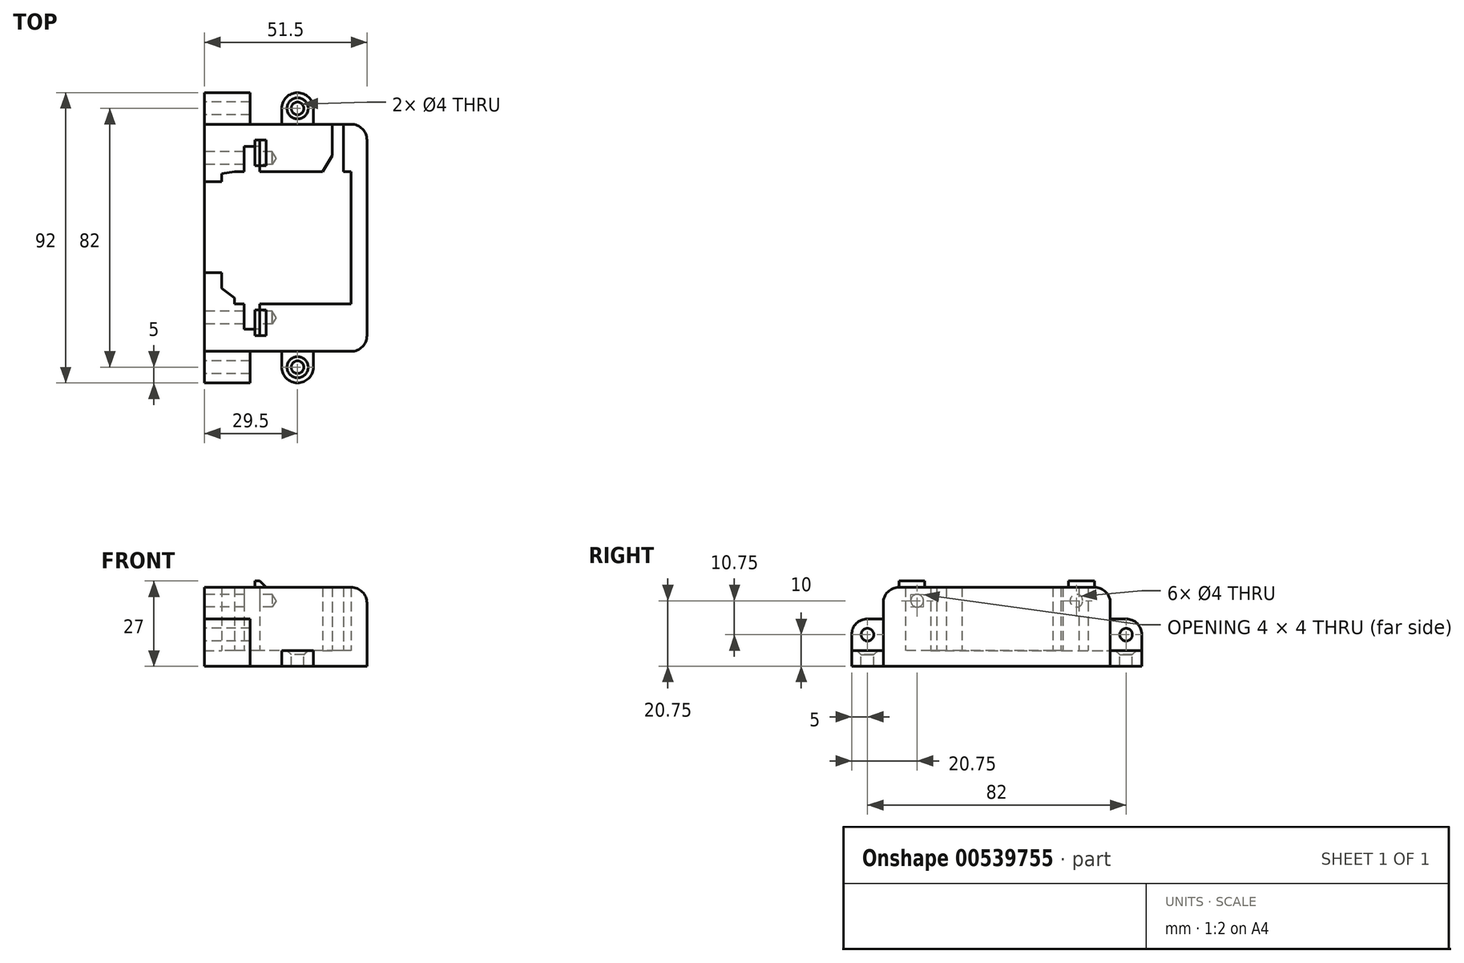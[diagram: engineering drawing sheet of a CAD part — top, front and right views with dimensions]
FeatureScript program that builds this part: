
annotation { "Feature Type Name" : "Feature", "Feature Type Description" : "" }
export const myFeature = defineFeature(function(context is Context, id is Id, definition is map)
    precondition{}
    {
        {
            var Q0;
            Q0=qCreatedBy(makeId("Top.planeOp"),FACE);
            var sketch = newSketch(context, id + "F0", { "sketchPlane" : qUnion([Q0])});
            skLineSegment(sketch, "E0.bottom", {"start": v(23.5, -36) * mm, "end": v(-23.5, -36) * mm});
            skLineSegment(sketch, "E0.top", {"start": v(23.5, 36) * mm, "end": v(-23.5, 36) * mm});
            skLineSegment(sketch, "E0.left", {"start": v(23.5, -36) * mm, "end": v(23.5, 36) * mm});
            skLineSegment(sketch, "E0.right", {"start": v(-23.5, -36) * mm, "end": v(-23.5, 0) * mm});
            skPoint(sketch, "E0.middle", {"position": v(0, 0) * mm});
            skLineSegment(sketch, "E1.bottom", {"start": v(18.5, -21) * mm, "end": v(-18.5, -21) * mm});
            skLineSegment(sketch, "E1.top", {"start": v(9.5, 21) * mm, "end": v(-18.5, 21) * mm});
            skLineSegment(sketch, "E1.left", {"start": v(18.5, -21) * mm, "end": v(18.5, 21) * mm});
            skLineSegment(sketch, "E1.right", {"start": v(-18.5, -21) * mm, "end": v(-18.5, 21) * mm, "construction": true});
            skLineSegment(sketch, "E2.right", {"start": v(12.5, 26) * mm, "end": v(12.5, 36) * mm});
            skLineSegment(sketch, "E3", {"start": v(-23.5, 0) * mm, "end": v(23.5, 0) * mm, "construction": true});
            skLineSegment(sketch, "E4.bottom", {"start": v(-10.5, 21) * mm, "end": v(-15.5, 21) * mm});
            skLineSegment(sketch, "E4.top", {"start": v(-10.5, 29) * mm, "end": v(-15.5, 29) * mm});
            skLineSegment(sketch, "E4.left", {"start": v(-10.5, 21) * mm, "end": v(-10.5, 29) * mm});
            skLineSegment(sketch, "E4.right", {"start": v(-15.5, 21) * mm, "end": v(-15.5, 29) * mm});
            skLineSegment(sketch, "E5.bottom", {"start": v(-10.5, -21) * mm, "end": v(-15.5, -21) * mm});
            skLineSegment(sketch, "E5.top", {"start": v(-10.5, -29) * mm, "end": v(-15.5, -29) * mm});
            skLineSegment(sketch, "E5.left", {"start": v(-10.5, -21) * mm, "end": v(-10.5, -29) * mm});
            skLineSegment(sketch, "E5.right", {"start": v(-15.5, -21) * mm, "end": v(-15.5, -29) * mm});
            skLineSegment(sketch, "E6.bottom", {"start": v(-18.5, 21) * mm, "end": v(-22.5, 20.3) * mm});
            skLineSegment(sketch, "E6.right", {"start": v(-22.5, 20.3) * mm, "end": v(-22.5, 17.8) * mm});
            skLineSegment(sketch, "E7", {"start": v(-22.5, -16) * mm, "end": v(-18.5, -19) * mm});
            skLineSegment(sketch, "E8.bottom", {"start": v(-23.5, 17.8) * mm, "end": v(-22.5, 17.8) * mm});
            skLineSegment(sketch, "E8.top", {"start": v(-23.5, -11) * mm, "end": v(-22.5, -11) * mm});
            skLineSegment(sketch, "E8.left", {"start": v(-23.5, 17.8) * mm, "end": v(-23.5, -11) * mm});
            skLineSegment(sketch, "E8.right", {"start": v(-22.5, 17.8) * mm, "end": v(-22.5, -11) * mm});
            skLineSegment(sketch, "E9.trimOffspring", {"start": v(-23.5, 17.8) * mm, "end": v(-23.5, 36) * mm});
            skLineSegment(sketch, "E10.trimOffspring", {"start": v(-22.5, 0) * mm, "end": v(-22.5, -16) * mm});
            skLineSegment(sketch, "E11", {"start": v(-18.5, -19) * mm, "end": v(-18.5, -21) * mm});
            skLineSegment(sketch, "E12", {"start": v(9.5, 21) * mm, "end": v(12.5, 26) * mm});
            skLineSegment(sketch, "E13", {"start": v(18.5, 21) * mm, "end": v(16, 21) * mm});
            skLineSegment(sketch, "E14", {"start": v(16, 21) * mm, "end": v(16, 36) * mm});
            skSolve(sketch);
        }
        {
            var Q0;
            Q0=makeQuery(id+"F0.imprint","IMPRINT",FACE,{"disambiguationData":[TD([[makeQuery(id+"F0.imprint","IMPRINT",EDGE,{"derivedFrom":sQuery(id+"F0.wireOp",EDGE,"E0.bottom")}),-1.0]])]});
            var Q1;
            {var subQ5=sQuery(id+"F0.wireOp",EDGE,"E2.right");Q1=makeQuery(id+"F0.imprint","IMPRINT",FACE,{"disambiguationData":[TD([[makeQuery(id+"F0.imprint","IMPRINT",EDGE,{"derivedFrom":subQ5}),1.0]])]});}
            extrude(context, id + "F1", {"entities" : qUnion([Q0, Q1]), "depth" : 20 * mm, "offsetDistance" : 25 * mm});
        }
        {
            var Q0;
            {var subQ2=sQuery(id+"F0.wireOp",EDGE,"E1.left");Q0=makeQuery(id+"F0.imprint","IMPRINT",FACE,{"disambiguationData":[TD([[makeQuery(id+"F0.imprint","IMPRINT",EDGE,{"derivedFrom":subQ2}),1.0]])]});}
            var sketch = newSketch(context, id + "F2", { "sketchPlane" : qUnion([Q0])});
            skLineSegment(sketch, "E15.bottom", {"start": v(23.5, 36) * mm, "end": v(-23.5, 36) * mm});
            skLineSegment(sketch, "E15.top", {"start": v(23.5, -36) * mm, "end": v(-23.5, -36) * mm});
            skLineSegment(sketch, "E15.left", {"start": v(23.5, 36) * mm, "end": v(23.5, -36) * mm});
            skLineSegment(sketch, "E15.right", {"start": v(-23.5, 36) * mm, "end": v(-23.5, -36) * mm});
            skPoint(sketch, "E15.middle", {"position": v(0, 0) * mm});
            skSolve(sketch);
        }
        {
            var Q0;
            Q0=makeQuery(id+"F2.imprint","IMPRINT",FACE,{"disambiguationData":[TD([[makeQuery(id+"F2.imprint","IMPRINT",EDGE,{"derivedFrom":sQuery(id+"F2.wireOp",EDGE,"E15.bottom")}),1.0]])]});
            var Q1;
            {var subQ3=sQuery(id+"F0.wireOp",EDGE,"E1.left");Q1=makeQuery(id+"F2.imprint","IMPRINT",FACE,{"disambiguationData":[TD([[makeQuery(id+"F2.imprint","IMPRINT",EDGE,{"derivedFrom":makeQuery(id+"F0.imprint","IMPRINT",EDGE,{"derivedFrom":subQ3})}),1.0]])]});}
            extrude(context, id + "F3", {"entities" : qUnion([Q0, Q1]), "oppositeDirection" : true, "depth" : 5 * mm, "offsetDistance" : 25 * mm});
        }
        {
            var Q0;
            Q0=makeQuery(id+"F1.opExtrude","SWEPT_BODY",BODY,{"disambiguationData":[OSD([sQuery(id+"F0.wireOp",EDGE,"E0.top"),sQuery(id+"F0.wireOp",EDGE,"E1.top"),sQuery(id+"F0.wireOp",EDGE,"E2.right"),sQuery(id+"F0.wireOp",EDGE,"E4.top"),sQuery(id+"F0.wireOp",EDGE,"E4.left"),sQuery(id+"F0.wireOp",EDGE,"E4.right"),sQuery(id+"F0.wireOp",EDGE,"E6.bottom"),sQuery(id+"F0.wireOp",EDGE,"E6.right"),sQuery(id+"F0.wireOp",EDGE,"E8.bottom"),sQuery(id+"F0.wireOp",EDGE,"E9.trimOffspring")])]});
            var Q1;
            Q1=makeQuery(id+"F3.opExtrude","SWEPT_BODY",BODY,{"disambiguationData":[OSD([sQuery(id+"F2.wireOp",EDGE,"E15.bottom"),sQuery(id+"F2.wireOp",EDGE,"E15.top"),sQuery(id+"F2.wireOp",EDGE,"E15.left"),sQuery(id+"F2.wireOp",EDGE,"E15.right")])]});
            var Q2;
            Q2=makeQuery(id+"F1.opExtrude","SWEPT_BODY",BODY,{"disambiguationData":[OSD([sQuery(id+"F0.wireOp",EDGE,"E0.bottom"),sQuery(id+"F0.wireOp",EDGE,"E0.top"),sQuery(id+"F0.wireOp",EDGE,"E0.left"),sQuery(id+"F0.wireOp",EDGE,"E0.right"),sQuery(id+"F0.wireOp",EDGE,"E1.bottom"),sQuery(id+"F0.wireOp",EDGE,"E1.left"),sQuery(id+"F0.wireOp",EDGE,"E2.left"),sQuery(id+"F0.wireOp",EDGE,"E5.top"),sQuery(id+"F0.wireOp",EDGE,"E5.left"),sQuery(id+"F0.wireOp",EDGE,"E5.right"),sQuery(id+"F0.wireOp",EDGE,"E7"),sQuery(id+"F0.wireOp",EDGE,"E8.top"),sQuery(id+"F0.wireOp",EDGE,"E10.trimOffspring"),sQuery(id+"F0.wireOp",EDGE,"E11")])]});
            booleanBodies(context, id + "F4", {"operationType" : BooleanOperationType.UNION, "tools" : qUnion([Q0, Q1, Q2])});
        }
        {
            var Q0;
            Q0=makeQuery(id+"F4.opBoolean","MERGE",FACE,{"derivedFrom":[makeQuery(id+"F1.opExtrude","SWEPT_FACE",FACE,{"disambiguationData":[OSD([sQuery(id+"F0.wireOp",EDGE,"E0.bottom")])]}),makeQuery(id+"F3.opExtrude","SWEPT_FACE",FACE,{"disambiguationData":[OSD([sQuery(id+"F2.wireOp",EDGE,"E15.top")])]})]});
            var sketch = newSketch(context, id + "F5", { "sketchPlane" : qUnion([Q0])});
            skLineSegment(sketch, "E16.bottom", {"start": v(-23.5, -5) * mm, "end": v(-13.5, -5) * mm});
            skLineSegment(sketch, "E16.top", {"start": v(-23.5, 10) * mm, "end": v(-13.5, 10) * mm});
            skLineSegment(sketch, "E16.left", {"start": v(-23.5, -5) * mm, "end": v(-23.5, 10) * mm});
            skLineSegment(sketch, "E16.right", {"start": v(-13.5, -5) * mm, "end": v(-13.5, 10) * mm});
            skSolve(sketch);
        }
        {
            var Q0;
            Q0=makeQuery(id+"F5.imprint","IMPRINT",FACE,{"disambiguationData":[TD([[makeQuery(id+"F5.imprint","IMPRINT",EDGE,{"derivedFrom":sQuery(id+"F5.wireOp",EDGE,"E16.bottom")}),-1.0]])]});
            extrude(context, id + "F6", {"entities" : qUnion([Q0]), "operationType" : NewBodyOperationType.ADD, "depth" : 10 * mm, "offsetDistance" : 25 * mm});
        }
        {
            var Q0;
            Q0=makeQuery(id+"F6.opExtrude","CAP_EDGE",EDGE,{"disambiguationData":[OSD([sQuery(id+"F5.wireOp",EDGE,"E16.top")])],"isStart":false});
            fillet(context, id + "F7", {"entities" : qUnion([Q0]), "radius" : 5 * mm, "tangentPropagation" : true, "allowEdgeOverflow" : false});
        }
        {
            var Q0;
            {var subQ0=sQuery(id+"F0.wireOp",EDGE,"E0.top");Q0=makeQuery(id+"F4.opBoolean","MERGE",FACE,{"derivedFrom":[makeQuery(id+"F1.opExtrude","SWEPT_FACE",FACE,{"disambiguationData":[OSD([subQ0]),TDD([makeQuery(id+"F0.imprint","IMPRINT",EDGE,{"disambiguationData":[TD([[makeQuery(id+"F0.imprint","INTERSECT",VERTEX,{"derivedFrom":[subQ0,sQuery(id+"F0.wireOp",EDGE,"E0.left")]}),-1.0]])],"derivedFrom":subQ0})])]}),makeQuery(id+"F1.opExtrude","SWEPT_FACE",FACE,{"disambiguationData":[OSD([subQ0]),TDD([makeQuery(id+"F0.imprint","IMPRINT",EDGE,{"disambiguationData":[TD([[makeQuery(id+"F0.imprint","INTERSECT",VERTEX,{"derivedFrom":[subQ0,sQuery(id+"F0.wireOp",EDGE,"E9.trimOffspring")]}),1.0]])],"derivedFrom":subQ0})])]}),makeQuery(id+"F3.opExtrude","SWEPT_FACE",FACE,{"disambiguationData":[OSD([sQuery(id+"F2.wireOp",EDGE,"E15.bottom")])]})]});}
            var sketch = newSketch(context, id + "F8", { "sketchPlane" : qUnion([Q0])});
            skLineSegment(sketch, "E17.bottom", {"start": v(23.5, -5) * mm, "end": v(13.5, -5) * mm});
            skLineSegment(sketch, "E17.top", {"start": v(23.5, 10) * mm, "end": v(13.5, 10) * mm});
            skLineSegment(sketch, "E17.left", {"start": v(23.5, -5) * mm, "end": v(23.5, 10) * mm});
            skLineSegment(sketch, "E17.right", {"start": v(13.5, -5) * mm, "end": v(13.5, 10) * mm});
            skSolve(sketch);
        }
        {
            var Q0;
            Q0=makeQuery(id+"F8.imprint","IMPRINT",FACE,{"disambiguationData":[TD([[makeQuery(id+"F8.imprint","IMPRINT",EDGE,{"derivedFrom":sQuery(id+"F8.wireOp",EDGE,"E17.bottom")}),1.0]])]});
            extrude(context, id + "F9", {"entities" : qUnion([Q0]), "operationType" : NewBodyOperationType.ADD, "depth" : 10 * mm, "offsetDistance" : 25 * mm});
        }
        {
            var Q0;
            Q0=makeQuery(id+"F9.opExtrude","CAP_EDGE",EDGE,{"disambiguationData":[OSD([sQuery(id+"F8.wireOp",EDGE,"E17.top")])],"isStart":false});
            fillet(context, id + "F10", {"entities" : qUnion([Q0]), "radius" : 5 * mm, "tangentPropagation" : true, "allowEdgeOverflow" : false});
        }
        {
            var Q0;
            Q0=makeQuery(id+"F9.boolean.opBoolean","MERGE",FACE,{"derivedFrom":[makeQuery(id+"F6.boolean.opBoolean","MERGE",FACE,{"derivedFrom":[makeQuery(id+"F4.opBoolean","MERGE",FACE,{"derivedFrom":[makeQuery(id+"F1.opExtrude","SWEPT_FACE",FACE,{"disambiguationData":[OSD([sQuery(id+"F0.wireOp",EDGE,"E0.right")])]}),makeQuery(id+"F1.opExtrude","SWEPT_FACE",FACE,{"disambiguationData":[OSD([sQuery(id+"F0.wireOp",EDGE,"E9.trimOffspring")])]}),makeQuery(id+"F3.opExtrude","SWEPT_FACE",FACE,{"disambiguationData":[OSD([sQuery(id+"F2.wireOp",EDGE,"E15.right")])]})]}),makeQuery(id+"F6.opExtrude","SWEPT_FACE",FACE,{"disambiguationData":[OSD([sQuery(id+"F5.wireOp",EDGE,"E16.left")])]})]}),makeQuery(id+"F9.opExtrude","SWEPT_FACE",FACE,{"disambiguationData":[OSD([sQuery(id+"F8.wireOp",EDGE,"E17.left")])]})]});
            var sketch = newSketch(context, id + "F11", { "sketchPlane" : qUnion([Q0])});
            skPoint(sketch, "E18", {"position": v(-41, 5) * mm});
            skPoint(sketch, "E19", {"position": v(41, 5) * mm});
            skSolve(sketch);
        }
        {
            var Q0;
            Q0=sQuery(id+"F11.wireOp",VERTEX,"E18");
            var Q1;
            Q1=sQuery(id+"F11.wireOp",VERTEX,"E19");
            var Q2;
            Q2=makeQuery(id+"F1.opExtrude","SWEPT_BODY",BODY,{"disambiguationData":[OSD([sQuery(id+"F0.wireOp",EDGE,"E0.top"),sQuery(id+"F0.wireOp",EDGE,"E1.top"),sQuery(id+"F0.wireOp",EDGE,"E2.right"),sQuery(id+"F0.wireOp",EDGE,"E4.top"),sQuery(id+"F0.wireOp",EDGE,"E4.left"),sQuery(id+"F0.wireOp",EDGE,"E4.right"),sQuery(id+"F0.wireOp",EDGE,"E6.bottom"),sQuery(id+"F0.wireOp",EDGE,"E6.right"),sQuery(id+"F0.wireOp",EDGE,"E8.bottom"),sQuery(id+"F0.wireOp",EDGE,"E9.trimOffspring")])]});
            hole(context, id + "F12", {"style" : HoleStyle.SIMPLE, "endStyle" : HoleEndStyle.THROUGH, "holeDiameter" : 4 * mm, "isTappedThrough" : true, "tappedDepth" : 12 * mm, "tapClearance" : 3, "locations" : qUnion([Q0, Q1]), "scope" : qUnion([Q2])});
        }
        {
            var Q0;
            Q0=makeQuery(id+"F9.boolean.opBoolean","MERGE",FACE,{"derivedFrom":[makeQuery(id+"F6.boolean.opBoolean","MERGE",FACE,{"derivedFrom":[makeQuery(id+"F4.opBoolean","MERGE",FACE,{"derivedFrom":[makeQuery(id+"F1.opExtrude","SWEPT_FACE",FACE,{"disambiguationData":[OSD([sQuery(id+"F0.wireOp",EDGE,"E0.right")])]}),makeQuery(id+"F1.opExtrude","SWEPT_FACE",FACE,{"disambiguationData":[OSD([sQuery(id+"F0.wireOp",EDGE,"E9.trimOffspring")])]}),makeQuery(id+"F3.opExtrude","SWEPT_FACE",FACE,{"disambiguationData":[OSD([sQuery(id+"F2.wireOp",EDGE,"E15.right")])]})]}),makeQuery(id+"F6.opExtrude","SWEPT_FACE",FACE,{"disambiguationData":[OSD([sQuery(id+"F5.wireOp",EDGE,"E16.left")])]})]}),makeQuery(id+"F9.opExtrude","SWEPT_FACE",FACE,{"disambiguationData":[OSD([sQuery(id+"F8.wireOp",EDGE,"E17.left")])]})]});
            var sketch = newSketch(context, id + "F13", { "sketchPlane" : qUnion([Q0])});
            skPoint(sketch, "E20", {"position": v(25.25, 15.75) * mm});
            skPoint(sketch, "E21", {"position": v(-25.25, 15.75) * mm});
            skSolve(sketch);
        }
        {
            var Q0;
            Q0=sQuery(id+"F13.wireOp",VERTEX,"E21");
            var Q1;
            Q1=sQuery(id+"F13.wireOp",VERTEX,"E20");
            var Q2;
            Q2=makeQuery(id+"F1.opExtrude","SWEPT_BODY",BODY,{"disambiguationData":[OSD([sQuery(id+"F0.wireOp",EDGE,"E0.top"),sQuery(id+"F0.wireOp",EDGE,"E1.top"),sQuery(id+"F0.wireOp",EDGE,"E2.right"),sQuery(id+"F0.wireOp",EDGE,"E4.top"),sQuery(id+"F0.wireOp",EDGE,"E4.left"),sQuery(id+"F0.wireOp",EDGE,"E4.right"),sQuery(id+"F0.wireOp",EDGE,"E6.bottom"),sQuery(id+"F0.wireOp",EDGE,"E6.right"),sQuery(id+"F0.wireOp",EDGE,"E8.bottom"),sQuery(id+"F0.wireOp",EDGE,"E9.trimOffspring")])]});
            hole(context, id + "F14", {"style" : HoleStyle.SIMPLE, "endStyle" : HoleEndStyle.BLIND, "holeDiameter" : 4 * mm, "holeDepth" : 17 * mm, "isTappedThrough" : true, "tappedDepth" : 12 * mm, "tapClearance" : 3, "locations" : qUnion([Q0, Q1]), "scope" : qUnion([Q2])});
        }
        {
            var Q0;
            {var subQ0=sQuery(id+"F0.wireOp",EDGE,"E0.top");Q0=makeQuery(id+"F1.opExtrude","CAP_EDGE",EDGE,{"disambiguationData":[OSD([subQ0]),TDD([makeQuery(id+"F0.imprint","IMPRINT",EDGE,{"disambiguationData":[TD([[makeQuery(id+"F0.imprint","INTERSECT",VERTEX,{"derivedFrom":[subQ0,sQuery(id+"F0.wireOp",EDGE,"E9.trimOffspring")]}),1.0]])],"derivedFrom":subQ0})])],"isStart":false});}
            var Q1;
            Q1=makeQuery(id+"F1.opExtrude","CAP_EDGE",EDGE,{"disambiguationData":[OSD([sQuery(id+"F0.wireOp",EDGE,"E0.bottom")])],"isStart":false});
            var Q2;
            Q2=makeQuery(id+"F1.opExtrude","CAP_EDGE",EDGE,{"disambiguationData":[OSD([sQuery(id+"F0.wireOp",EDGE,"E0.left")])],"isStart":false});
            fillet(context, id + "F15", {"entities" : qUnion([Q0, Q1, Q2]), "radius" : 5 * mm, "tangentPropagation" : true, "allowEdgeOverflow" : false});
        }
        {
            var Q0;
            {var subQ0=sQuery(id+"F0.wireOp",EDGE,"E0.top");var subQ1=sQuery(id+"F0.wireOp",EDGE,"E0.left");Q0=makeQuery(id+"F15.opFillet","BLEND_EDGE",EDGE,{"blendedFrom":[makeQuery(id+"F1.opExtrude","CAP_EDGE",EDGE,{"disambiguationData":[OSD([subQ1])],"isStart":false}),makeQuery(id+"F4.opBoolean","MERGE",FACE,{"derivedFrom":[makeQuery(id+"F1.opExtrude","SWEPT_FACE",FACE,{"disambiguationData":[OSD([subQ0]),TDD([makeQuery(id+"F0.imprint","IMPRINT",EDGE,{"disambiguationData":[TD([[makeQuery(id+"F0.imprint","INTERSECT",VERTEX,{"derivedFrom":[subQ0,subQ1]}),-1.0]])],"derivedFrom":subQ0})])]}),makeQuery(id+"F1.opExtrude","SWEPT_FACE",FACE,{"disambiguationData":[OSD([subQ0]),TDD([makeQuery(id+"F0.imprint","IMPRINT",EDGE,{"disambiguationData":[TD([[makeQuery(id+"F0.imprint","INTERSECT",VERTEX,{"derivedFrom":[subQ0,sQuery(id+"F0.wireOp",EDGE,"E9.trimOffspring")]}),1.0]])],"derivedFrom":subQ0})])]}),makeQuery(id+"F3.opExtrude","SWEPT_FACE",FACE,{"disambiguationData":[OSD([sQuery(id+"F2.wireOp",EDGE,"E15.bottom")])]})]})],"blendedInto":[makeQuery(id+"F4.opBoolean","MERGE",FACE,{"derivedFrom":[makeQuery(id+"F1.opExtrude","SWEPT_FACE",FACE,{"disambiguationData":[OSD([subQ0]),TDD([makeQuery(id+"F0.imprint","IMPRINT",EDGE,{"disambiguationData":[TD([[makeQuery(id+"F0.imprint","INTERSECT",VERTEX,{"derivedFrom":[subQ0,subQ1]}),-1.0]])],"derivedFrom":subQ0})])]}),makeQuery(id+"F1.opExtrude","SWEPT_FACE",FACE,{"disambiguationData":[OSD([subQ0]),TDD([makeQuery(id+"F0.imprint","IMPRINT",EDGE,{"disambiguationData":[TD([[makeQuery(id+"F0.imprint","INTERSECT",VERTEX,{"derivedFrom":[subQ0,sQuery(id+"F0.wireOp",EDGE,"E9.trimOffspring")]}),1.0]])],"derivedFrom":subQ0})])]}),makeQuery(id+"F3.opExtrude","SWEPT_FACE",FACE,{"disambiguationData":[OSD([sQuery(id+"F2.wireOp",EDGE,"E15.bottom")])]})]})]});}
            var Q1;
            Q1=makeQuery(id+"F15.opFillet","BLEND_EDGE",EDGE,{"blendedFrom":[makeQuery(id+"F1.opExtrude","CAP_EDGE",EDGE,{"disambiguationData":[OSD([sQuery(id+"F0.wireOp",EDGE,"E0.bottom")])],"isStart":false}),makeQuery(id+"F1.opExtrude","CAP_EDGE",EDGE,{"disambiguationData":[OSD([sQuery(id+"F0.wireOp",EDGE,"E0.left")])],"isStart":false})],"blendedInto":[]});
            fillet(context, id + "F16", {"entities" : qUnion([Q0, Q1]), "radius" : 5 * mm, "tangentPropagation" : true, "allowEdgeOverflow" : false});
        }
        {
            var Q0;
            Q0=makeQuery(id+"F15.opFillet","SPLIT",FACE,{"disambiguationData":[OD(0.0)],"derivedFrom":makeQuery(id+"F1.opExtrude","CAP_FACE",FACE,{"disambiguationData":[OSD([sQuery(id+"F0.wireOp",EDGE,"E0.bottom"),sQuery(id+"F0.wireOp",EDGE,"E0.top"),sQuery(id+"F0.wireOp",EDGE,"E0.left"),sQuery(id+"F0.wireOp",EDGE,"E0.right"),sQuery(id+"F0.wireOp",EDGE,"E1.bottom"),sQuery(id+"F0.wireOp",EDGE,"E1.left"),sQuery(id+"F0.wireOp",EDGE,"E5.top"),sQuery(id+"F0.wireOp",EDGE,"E5.left"),sQuery(id+"F0.wireOp",EDGE,"E5.right"),sQuery(id+"F0.wireOp",EDGE,"E7"),sQuery(id+"F0.wireOp",EDGE,"E8.top"),sQuery(id+"F0.wireOp",EDGE,"E10.trimOffspring"),sQuery(id+"F0.wireOp",EDGE,"E11"),sQuery(id+"F0.wireOp",EDGE,"E13"),sQuery(id+"F0.wireOp",EDGE,"E14")])],"isStart":false})});
            var sketch = newSketch(context, id + "F17", { "sketchPlane" : qUnion([Q0])});
            skLineSegment(sketch, "E22", {"start": v(0, 0) * mm, "end": v(57.27, 0) * mm, "construction": true});
            skLineSegment(sketch, "E23.bottom", {"start": v(-10.5, -22.8) * mm, "end": v(-8.5, -22.8) * mm});
            skLineSegment(sketch, "E23.top", {"start": v(-10.5, -31) * mm, "end": v(-8.5, -31) * mm});
            skLineSegment(sketch, "E23.left", {"start": v(-10.5, -22.8) * mm, "end": v(-10.5, -31) * mm});
            skLineSegment(sketch, "E23.right", {"start": v(-8.5, -22.8) * mm, "end": v(-8.5, -31) * mm});
            skLineSegment(sketch, "E24.MirrorCS", {"start": v(-10.5, 22.8) * mm, "end": v(-8.5, 22.8) * mm});
            skLineSegment(sketch, "E25.MirrorCS", {"start": v(-10.5, 22.8) * mm, "end": v(-10.5, 31) * mm});
            skLineSegment(sketch, "E26.MirrorCS", {"start": v(-10.5, 31) * mm, "end": v(-8.5, 31) * mm});
            skLineSegment(sketch, "E27.MirrorCS", {"start": v(-8.5, 22.8) * mm, "end": v(-8.5, 31) * mm});
            skLineSegment(sketch, "E28.0", {"start": v(-15.5, -21) * mm, "end": v(-15.5, -29) * mm});
            skLineSegment(sketch, "E29.0", {"start": v(-10.5, -21) * mm, "end": v(-10.5, -29) * mm});
            skSolve(sketch);
        }
        {
            var Q0;
            Q0=makeQuery(id+"F17.imprint","IMPRINT",FACE,{"disambiguationData":[TD([[makeQuery(id+"F17.imprint","IMPRINT",EDGE,{"derivedFrom":sQuery(id+"F17.wireOp",EDGE,"E23.bottom")}),-1.0]])]});
            var Q1;
            Q1=makeQuery(id+"F17.imprint","IMPRINT",FACE,{"disambiguationData":[TD([[makeQuery(id+"F17.imprint","IMPRINT",EDGE,{"derivedFrom":sQuery(id+"F17.wireOp",EDGE,"E24.MirrorCS")}),1.0]])]});
            extrude(context, id + "F18", {"entities" : qUnion([Q0, Q1]), "operationType" : NewBodyOperationType.ADD, "depth" : 2 * mm, "offsetDistance" : 25 * mm});
        }
        {
            var Q0;
            Q0=makeQuery(id+"F18.boolean.opBoolean","MERGE",FACE,{"derivedFrom":[makeQuery(id+"F1.opExtrude","SWEPT_FACE",FACE,{"disambiguationData":[OSD([sQuery(id+"F0.wireOp",EDGE,"E4.left")])]}),makeQuery(id+"F18.opExtrude","SWEPT_FACE",FACE,{"disambiguationData":[OSD([sQuery(id+"F17.wireOp",EDGE,"E25.MirrorCS")])]})]});
            var sketch = newSketch(context, id + "F19", { "sketchPlane" : qUnion([Q0])});
            skLineSegment(sketch, "E30.bottom", {"start": v(-31, 22) * mm, "end": v(-22.8, 22) * mm});
            skLineSegment(sketch, "E30.top", {"start": v(-31, 20) * mm, "end": v(-22.8, 20) * mm});
            skLineSegment(sketch, "E30.left", {"start": v(-31, 22) * mm, "end": v(-31, 20) * mm});
            skLineSegment(sketch, "E30.right", {"start": v(-22.8, 22) * mm, "end": v(-22.8, 20) * mm});
            skLineSegment(sketch, "E31.MirrorCS", {"start": v(22.8, 22) * mm, "end": v(22.8, 20) * mm});
            skLineSegment(sketch, "E32.MirrorCS", {"start": v(31, 22) * mm, "end": v(31, 20) * mm});
            skLineSegment(sketch, "E33.MirrorCS", {"start": v(31, 20) * mm, "end": v(22.8, 20) * mm});
            skLineSegment(sketch, "E34.MirrorCS", {"start": v(31, 22) * mm, "end": v(22.8, 22) * mm});
            skSolve(sketch);
        }
        {
            var Q0;
            Q0=makeQuery(id+"F19.imprint","IMPRINT",FACE,{"disambiguationData":[TD([[makeQuery(id+"F19.imprint","IMPRINT",EDGE,{"derivedFrom":sQuery(id+"F19.wireOp",EDGE,"E30.bottom")}),1.0]])]});
            var Q1;
            Q1=makeQuery(id+"F19.imprint","IMPRINT",FACE,{"disambiguationData":[TD([[makeQuery(id+"F19.imprint","IMPRINT",EDGE,{"derivedFrom":sQuery(id+"F19.wireOp",EDGE,"E31.MirrorCS")}),1.0]])]});
            extrude(context, id + "F20", {"entities" : qUnion([Q0, Q1]), "operationType" : NewBodyOperationType.ADD, "depth" : 1.5 * mm, "offsetDistance" : 25 * mm});
        }
        {
            var Q0;
            Q0=makeQuery(id+"F18.opExtrude","CAP_EDGE",EDGE,{"disambiguationData":[OSD([sQuery(id+"F17.wireOp",EDGE,"E23.right")])],"isStart":false});
            var Q1;
            Q1=makeQuery(id+"F18.opExtrude","CAP_EDGE",EDGE,{"disambiguationData":[OSD([sQuery(id+"F17.wireOp",EDGE,"E27.MirrorCS")])],"isStart":false});
            chamfer(context, id + "F21", {"entities" : qUnion([Q0, Q1]), "width" : 2 * mm, "tangentPropagation" : true});
        }
        {
            var Q0;
            Q0=makeQuery(id+"F9.boolean.opBoolean","MERGE",FACE,{"derivedFrom":[makeQuery(id+"F6.boolean.opBoolean","MERGE",FACE,{"derivedFrom":[makeQuery(id+"F4.opBoolean","MERGE",FACE,{"derivedFrom":[makeQuery(id+"F1.opExtrude","SWEPT_FACE",FACE,{"disambiguationData":[OSD([sQuery(id+"F0.wireOp",EDGE,"E0.right")])]}),makeQuery(id+"F1.opExtrude","SWEPT_FACE",FACE,{"disambiguationData":[OSD([sQuery(id+"F0.wireOp",EDGE,"E9.trimOffspring")])]}),makeQuery(id+"F3.opExtrude","SWEPT_FACE",FACE,{"disambiguationData":[OSD([sQuery(id+"F2.wireOp",EDGE,"E15.right")])]})]}),makeQuery(id+"F6.opExtrude","SWEPT_FACE",FACE,{"disambiguationData":[OSD([sQuery(id+"F5.wireOp",EDGE,"E16.left")])]})]}),makeQuery(id+"F9.opExtrude","SWEPT_FACE",FACE,{"disambiguationData":[OSD([sQuery(id+"F8.wireOp",EDGE,"E17.left")])]})]});
            extrude(context, id + "F22", {"entities" : qUnion([Q0]), "operationType" : NewBodyOperationType.ADD, "depth" : 4.5 * mm, "offsetDistance" : 25 * mm});
        }
        {
            var Q0;
            {var subQ0=sQuery(id+"F8.wireOp",EDGE,"E17.bottom");var subQ1=sQuery(id+"F5.wireOp",EDGE,"E16.bottom");var subQ2=sQuery(id+"F2.wireOp",EDGE,"E15.right");Q0=makeQuery(id+"F22.boolean.opBoolean","MERGE",FACE,{"derivedFrom":[makeQuery(id+"F9.boolean.opBoolean","MERGE",FACE,{"derivedFrom":[makeQuery(id+"F6.boolean.opBoolean","MERGE",FACE,{"derivedFrom":[makeQuery(id+"F3.opExtrude","CAP_FACE",FACE,{"disambiguationData":[OSD([sQuery(id+"F2.wireOp",EDGE,"E15.bottom"),sQuery(id+"F2.wireOp",EDGE,"E15.top"),sQuery(id+"F2.wireOp",EDGE,"E15.left"),subQ2])],"isStart":false}),makeQuery(id+"F6.opExtrude","SWEPT_FACE",FACE,{"disambiguationData":[OSD([subQ1])]})]}),makeQuery(id+"F9.opExtrude","SWEPT_FACE",FACE,{"disambiguationData":[OSD([subQ0])]})]}),makeQuery(id+"F22.opExtrude","SWEPT_FACE",FACE,{"disambiguationData":[OSD([subQ2,subQ1,sQuery(id+"F5.wireOp",EDGE,"E16.left"),subQ0,sQuery(id+"F8.wireOp",EDGE,"E17.left")])]})]});}
            var sketch = newSketch(context, id + "F23", { "sketchPlane" : qUnion([Q0])});
            skLineSegment(sketch, "E35.bottom", {"start": v(-3.5, -36) * mm, "end": v(6.5, -36) * mm});
            skLineSegment(sketch, "E35.top", {"start": v(-3.5, -46) * mm, "end": v(6.5, -46) * mm});
            skLineSegment(sketch, "E35.left", {"start": v(-3.5, -36) * mm, "end": v(-3.5, -46) * mm});
            skLineSegment(sketch, "E35.right", {"start": v(6.5, -36) * mm, "end": v(6.5, -46) * mm});
            skPoint(sketch, "E36.centerSnap0", {"position": v(1.5, -46) * mm});
            skPoint(sketch, "E36.centerSnap1", {"position": v(6.5, -41) * mm});
            skLineSegment(sketch, "E37.MirrorCS", {"start": v(-3.5, 36) * mm, "end": v(6.5, 36) * mm});
            skLineSegment(sketch, "E38.MirrorCS", {"start": v(-3.5, 46) * mm, "end": v(6.5, 46) * mm});
            skLineSegment(sketch, "E39.MirrorCS", {"start": v(-3.5, 36) * mm, "end": v(-3.5, 46) * mm});
            skPoint(sketch, "E40.MirrorP", {"position": v(1.5, 46) * mm});
            skPoint(sketch, "E41.MirrorP", {"position": v(6.5, 41) * mm});
            skLineSegment(sketch, "E42.MirrorCS", {"start": v(6.5, 36) * mm, "end": v(6.5, 46) * mm});
            skPoint(sketch, "E43", {"position": v(1.5, -41) * mm});
            skPoint(sketch, "E44", {"position": v(1.5, 41) * mm});
            skSolve(sketch);
        }
        {
            var Q0;
            Q0=makeQuery(id+"F23.imprint","IMPRINT",FACE,{"disambiguationData":[TD([[makeQuery(id+"F23.imprint","IMPRINT",EDGE,{"derivedFrom":sQuery(id+"F23.wireOp",EDGE,"E35.bottom")}),1.0]])]});
            var Q1;
            Q1=makeQuery(id+"F23.imprint","IMPRINT",FACE,{"disambiguationData":[TD([[makeQuery(id+"F23.imprint","IMPRINT",EDGE,{"derivedFrom":sQuery(id+"F23.wireOp",EDGE,"E37.MirrorCS")}),-1.0]])]});
            extrude(context, id + "F24", {"entities" : qUnion([Q0, Q1]), "operationType" : NewBodyOperationType.ADD, "oppositeDirection" : true, "depth" : 5 * mm, "offsetDistance" : 25 * mm});
        }
        {
            var Q0;
            Q0=makeQuery(id+"F24.opExtrude","SWEPT_EDGE",EDGE,{"disambiguationData":[OSD([sQuery(id+"F23.wireOp",EDGE,"E38.MirrorCS"),sQuery(id+"F23.wireOp",EDGE,"E42.MirrorCS")])]});
            var Q1;
            Q1=makeQuery(id+"F24.opExtrude","SWEPT_EDGE",EDGE,{"disambiguationData":[OSD([sQuery(id+"F23.wireOp",EDGE,"E38.MirrorCS"),sQuery(id+"F23.wireOp",EDGE,"E39.MirrorCS")])]});
            var Q2;
            Q2=makeQuery(id+"F24.opExtrude","SWEPT_EDGE",EDGE,{"disambiguationData":[OSD([sQuery(id+"F23.wireOp",EDGE,"E35.top"),sQuery(id+"F23.wireOp",EDGE,"E35.right")])]});
            var Q3;
            Q3=makeQuery(id+"F24.opExtrude","SWEPT_EDGE",EDGE,{"disambiguationData":[OSD([sQuery(id+"F23.wireOp",EDGE,"E35.top"),sQuery(id+"F23.wireOp",EDGE,"E35.left")])]});
            fillet(context, id + "F25", {"entities" : qUnion([Q0, Q1, Q2, Q3]), "radius" : 5 * mm, "tangentPropagation" : true, "allowEdgeOverflow" : false});
        }
        {
            var Q0;
            Q0=makeQuery(id+"F24.opExtrude","CAP_FACE",FACE,{"disambiguationData":[OSD([sQuery(id+"F23.wireOp",EDGE,"E37.MirrorCS"),sQuery(id+"F23.wireOp",EDGE,"E38.MirrorCS"),sQuery(id+"F23.wireOp",EDGE,"E39.MirrorCS"),sQuery(id+"F23.wireOp",EDGE,"E42.MirrorCS")])],"isStart":false});
            var sketch = newSketch(context, id + "F26", { "sketchPlane" : qUnion([Q0])});
            skPoint(sketch, "E45", {"position": v(1.5, 41) * mm});
            skPoint(sketch, "E46.MirrorP", {"position": v(1.5, -41) * mm});
            skSolve(sketch);
        }
        {
            var Q0;
            Q0=sQuery(id+"F26.wireOp",VERTEX,"E46.MirrorP");
            var Q1;
            Q1=sQuery(id+"F26.wireOp",VERTEX,"E45");
            var Q2;
            Q2=makeQuery(id+"F1.opExtrude","SWEPT_BODY",BODY,{"disambiguationData":[OSD([sQuery(id+"F0.wireOp",EDGE,"E0.top"),sQuery(id+"F0.wireOp",EDGE,"E1.top"),sQuery(id+"F0.wireOp",EDGE,"E2.right"),sQuery(id+"F0.wireOp",EDGE,"E4.top"),sQuery(id+"F0.wireOp",EDGE,"E4.left"),sQuery(id+"F0.wireOp",EDGE,"E4.right"),sQuery(id+"F0.wireOp",EDGE,"E6.bottom"),sQuery(id+"F0.wireOp",EDGE,"E6.right"),sQuery(id+"F0.wireOp",EDGE,"E8.bottom"),sQuery(id+"F0.wireOp",EDGE,"E9.trimOffspring"),sQuery(id+"F0.wireOp",EDGE,"E12")])]});
            hole(context, id + "F27", {"style" : HoleStyle.C_SINK, "endStyle" : HoleEndStyle.THROUGH, "holeDiameter" : 4 * mm, "cSinkDiameter" : 6.72 * mm, "cSinkAngle" : 90 * degree, "majorDiameter" : 5 * mm, "isTappedThrough" : true, "tappedDepth" : 12 * mm, "tapClearance" : 3, "locations" : qUnion([Q0, Q1]), "scope" : qUnion([Q2])});
        }
    });
